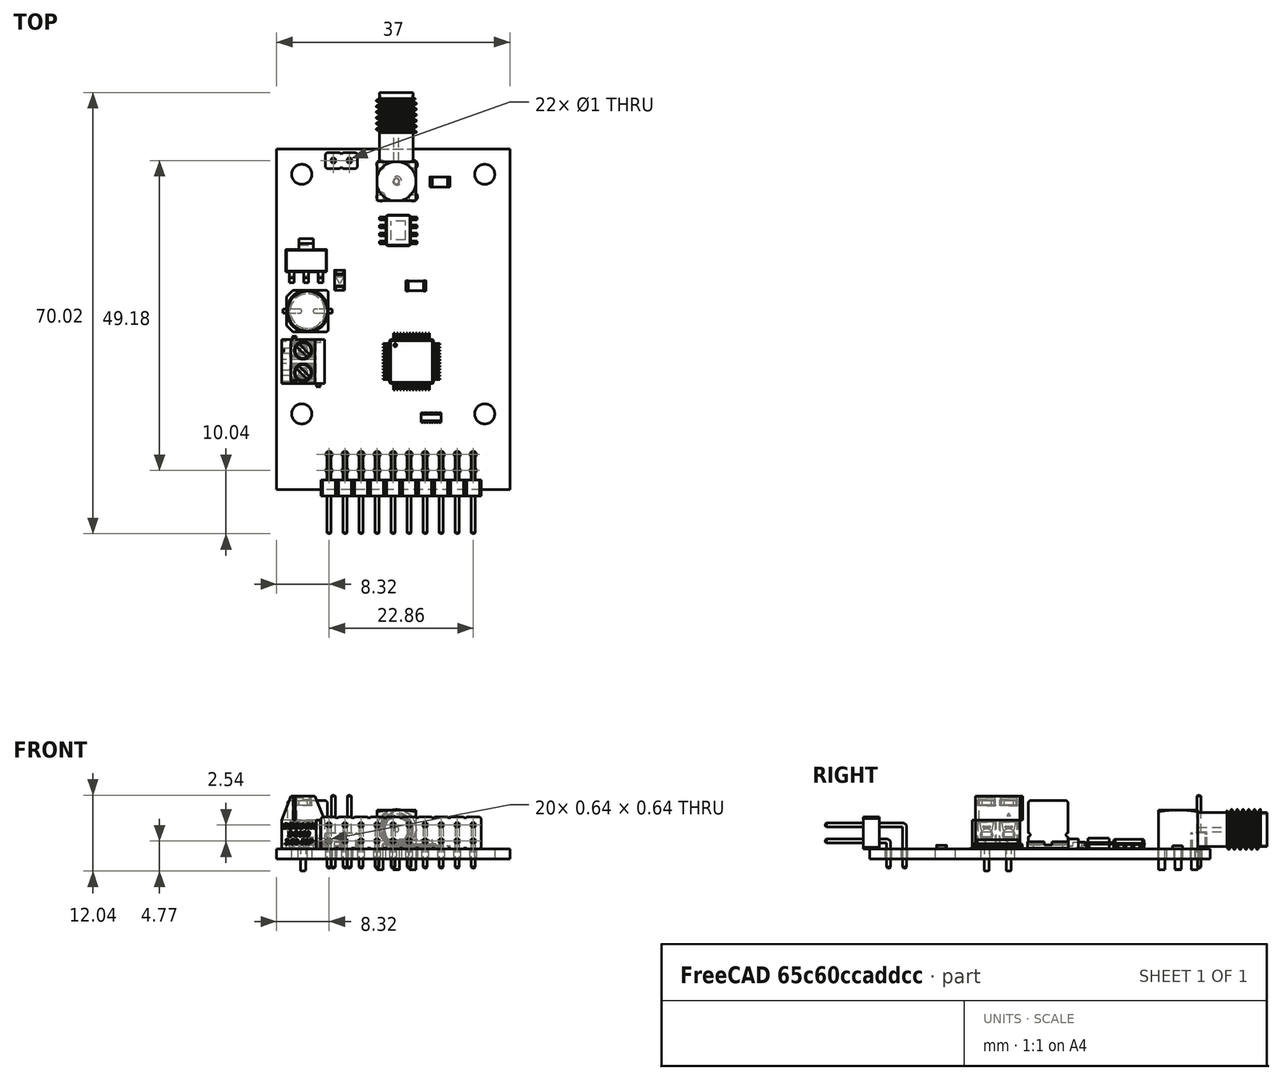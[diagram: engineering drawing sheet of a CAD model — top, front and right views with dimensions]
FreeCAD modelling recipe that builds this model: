
FCSTD DOCUMENT  (FreeCAD 1.0R39109 (Git))
Label: ADC
License: All rights reserved
LicenseURL: https://en.wikipedia.org/wiki/All_rights_reserved
objects: App::Link×34, Part::Feature×13, App::Part×4, PartDesign::CoordinateSystem×1, Sketcher::SketchObject×1
note: 16 computed .brp shape members not serialized (recipe doc carries the construction recipe); baked Part::Feature solids carry a one-line shape summary decoded from their .brp

FEATURE [PartDesign::CoordinateSystem] Local_CS_3770
  AttacherType = Attacher::AttachEngine3D
  MapMode = 2
FEATURE [Part::Feature] Pcb_3770
  Placement = pos=(-93.74,138.54,0) rot=(0,0,1;0rad)
  shape: bbox 37 x 54 x 1.6 mm, 39 faces (baked)
FEATURE [Sketcher::SketchObject] PCB_Sketch_3770
  ArcFitTolerance = 1e-06
  FullyConstrained = false
  MakeInternals = false
  sketch-geometry (4):
    g0: LineSegment StartX=-31.24 StartY=51.04 StartZ=0 EndX=5.76 EndY=51.04 EndZ=0
    g1: LineSegment StartX=5.76 StartY=51.04 StartZ=0 EndX=5.76 EndY=-2.96 EndZ=0
    g2: LineSegment StartX=5.76 StartY=-2.96 StartZ=0 EndX=-31.24 EndY=-2.96 EndZ=0
    g3: LineSegment StartX=-31.24 StartY=-2.96 StartZ=0 EndX=-31.24 EndY=51.04 EndZ=0
  constraints (4):
    c: Coincident(g2,g3)
    c: Coincident(g0,g3)
    c: Coincident(g1,g2)
    c: Coincident(g0,g1)
FEATURE [App::Part] Board_Geoms_3770
  Group = -> [Pcb_3770,PCB_Sketch_3770]
  Origin = -> Origin
FEATURE [Part::Feature] Shape  label="REF_R_1206_3216Metric_301ddd0c36ed"
  Placement = pos=(-5.34,45.84,0) rot=(0,0,1;0rad)
  shape: bbox 3.2 x 1.6 x 0.55 mm, 26 faces (baked)
FEATURE [App::Link] REF_R_1206_3216Metric_301ddd0c36ed_ln_  label="REF_REF_R_1206_3216Metric_70df84f1ae34"
  LinkPlacement = pos=(-22.84,41.94,0) rot=(0,0,1;1.5708rad)
  LinkedObject = -> Shape
  Placement = pos=(-22.84,41.94,0) rot=(0,0,1;1.5708rad)
FEATURE [App::Link] REF_R_1206_3216Metric_301ddd0c36ed_ln_001  label="REF_REF_R_1206_3216Metric_a6f854153131"
  LinkPlacement = pos=(1.16,14.24,0) rot=(0,0,1;0rad)
  LinkedObject = -> Shape
  Placement = pos=(1.16,14.24,0) rot=(0,0,1;0rad)
FEATURE [Part::Feature] Shape001  label="REF_C_1206_3216Metric_e221a3b84079"
  Placement = pos=(-9.14,29.34,0) rot=(0,0,1;0rad)
  shape: bbox 3.2 x 1.6 x 1.6 mm, 28 faces (baked)
FEATURE [App::Link] REF_R_1206_3216Metric_301ddd0c36ed_ln_002  label="REF_REF_R_1206_3216Metric_a0f92e46f677"
  LinkPlacement = pos=(-10.64,32.94,0) rot=(0,0,1;1.5708rad)
  LinkedObject = -> Shape
  Placement = pos=(-10.64,32.94,0) rot=(0,0,1;1.5708rad)
FEATURE [Part::Feature] Shape002  label="REF_CP_Elec_63x77_d1b758cef271"
  Placement = pos=(-26.34,25.34,0) rot=(0,0,1;0rad)
  shape: bbox 8.606 x 8.603 x 7.7 mm, 41 faces (baked)
FEATURE [App::Link] REF_R_1206_3216Metric_301ddd0c36ed_ln_003  label="REF_REF_R_1206_3216Metric_1b9d2568f397"
  LinkPlacement = pos=(-20.24,41.94,0) rot=(0,0,1;1.5708rad)
  LinkedObject = -> Shape
  Placement = pos=(-20.24,41.94,0) rot=(0,0,1;1.5708rad)
FEATURE [Part::Feature] Shape003  label="REF_SOIC-8-1EP_3.9x4.9mm_P1.27mm_EP2.29x3mm_4b1fed1f54c1"
  Placement = pos=(-11.94,38.14,0) rot=(0,0,1;3.14159rad)
  shape: bbox 6 x 4.9 x 1.55 mm, 152 faces (baked)
FEATURE [App::Link] REF_C_1206_3216Metric_e221a3b84079_ln_  label="REF_REF_C_1206_3216Metric_3e90dc9b15e9"
  LinkPlacement = pos=(-1.24,27.14,0) rot=(0,0,1;0rad)
  LinkedObject = -> Shape001
  Placement = pos=(-1.24,27.14,0) rot=(0,0,1;0rad)
FEATURE [App::Link] REF_C_1206_3216Metric_e221a3b84079_ln_001  label="REF_REF_C_1206_3216Metric_f21636db2d26"
  LinkPlacement = pos=(-7.14,24.54,0) rot=(0,0,1;0rad)
  LinkedObject = -> Shape001
  Placement = pos=(-7.14,24.54,0) rot=(0,0,1;0rad)
FEATURE [App::Link] REF_C_1206_3216Metric_e221a3b84079_ln_002  label="REF_REF_C_1206_3216Metric_18777c7b1951"
  LinkPlacement = pos=(-10.74,25.34,0) rot=(0,0,1;1.5708rad)
  LinkedObject = -> Shape001
  Placement = pos=(-10.74,25.34,0) rot=(0,0,1;1.5708rad)
FEATURE [App::Link] REF_R_1206_3216Metric_301ddd0c36ed_ln_004  label="REF_REF_R_1206_3216Metric_5a7a546a1d58"
  LinkPlacement = pos=(0.96,22.24,0) rot=(0,0,1;0rad)
  LinkedObject = -> Shape
  Placement = pos=(0.96,22.24,0) rot=(0,0,1;0rad)
FEATURE [App::Link] REF_R_1206_3216Metric_301ddd0c36ed_ln_005  label="REF_REF_R_1206_3216Metric_6cf90c486473"
  LinkPlacement = pos=(-18.04,8.54,0) rot=(0,0,1;1.5708rad)
  LinkedObject = -> Shape
  Placement = pos=(-18.04,8.54,0) rot=(0,0,1;1.5708rad)
FEATURE [Part::Feature] Shape004  label="REF_LED_1206_3216Metric_2fccf6a8874c"
  Placement = pos=(-21.24,30.24,0) rot=(0,0,1;1.5708rad)
  shape: bbox 1.6 x 3.2 x 1.1 mm, 50 faces (baked)
FEATURE [Part::Feature] Shape005  label="REF_PinHeader_1x02_P254mm_Vertical_da5b8ef0d3b1"
  Placement = pos=(-22.24,49.24,0) rot=(0,0,1;1.5708rad)
  shape: bbox 5.08 x 2.54 x 11.54 mm, 52 faces (baked)
FEATURE [App::Link] REF_C_1206_3216Metric_e221a3b84079_ln_003  label="REF_REF_C_1206_3216Metric_64c44e93813f"
  LinkPlacement = pos=(-16.44,19.84,0) rot=(0,0,1;1.5708rad)
  LinkedObject = -> Shape001
  Placement = pos=(-16.44,19.84,0) rot=(0,0,1;1.5708rad)
FEATURE [App::Link] REF_R_1206_3216Metric_301ddd0c36ed_ln_006  label="REF_REF_R_1206_3216Metric_3b6dfaf97a83"
  LinkPlacement = pos=(-5.34,48.74,0) rot=(0,0,1;0rad)
  LinkedObject = -> Shape
  Placement = pos=(-5.34,48.74,0) rot=(0,0,1;0rad)
FEATURE [App::Link] REF_R_1206_3216Metric_301ddd0c36ed_ln_007  label="REF_REF_R_1206_3216Metric_8c0fe4bfaf64"
  LinkPlacement = pos=(0.96,19.44,0) rot=(0,0,1;0rad)
  LinkedObject = -> Shape
  Placement = pos=(0.96,19.44,0) rot=(0,0,1;0rad)
FEATURE [App::Link] REF_C_1206_3216Metric_e221a3b84079_ln_004  label="REF_REF_C_1206_3216Metric_99c8eecee891"
  LinkPlacement = pos=(-13.14,25.34,0) rot=(0,0,1;1.5708rad)
  LinkedObject = -> Shape001
  Placement = pos=(-13.14,25.34,0) rot=(0,0,1;1.5708rad)
FEATURE [App::Link] REF_R_1206_3216Metric_301ddd0c36ed_ln_008  label="REF_REF_R_1206_3216Metric_75b0c98a4610"
  LinkPlacement = pos=(-6.34,35.04,0) rot=(0,0,1;1.5708rad)
  LinkedObject = -> Shape
  Placement = pos=(-6.34,35.04,0) rot=(0,0,1;1.5708rad)
FEATURE [App::Link] REF_C_1206_3216Metric_e221a3b84079_ln_005  label="REF_REF_C_1206_3216Metric_2542e80cc9ef"
  LinkPlacement = pos=(-4.74,29.34,0) rot=(0,0,1;0rad)
  LinkedObject = -> Shape001
  Placement = pos=(-4.74,29.34,0) rot=(0,0,1;0rad)
FEATURE [App::Link] REF_R_1206_3216Metric_301ddd0c36ed_ln_009  label="REF_REF_R_1206_3216Metric_7b8190f97f6e"
  LinkPlacement = pos=(-6.44,39.74,0) rot=(0,0,1;1.5708rad)
  LinkedObject = -> Shape
  Placement = pos=(-6.44,39.74,0) rot=(0,0,1;1.5708rad)
FEATURE [Part::Feature] Shape006  label="REF_R_Array_Concave_4x0603_6ebfddd59be7"
  Placement = pos=(-6.74,8.44,0) rot=(0,0,1;1.5708rad)
  shape: bbox 3.2 x 1.6 x 0.6 mm, 140 faces (baked)
FEATURE [App::Link] REF_C_1206_3216Metric_e221a3b84079_ln_006  label="REF_REF_C_1206_3216Metric_ddc78717e179"
  LinkPlacement = pos=(-2.54,20.84,0) rot=(0,0,1;1.5708rad)
  LinkedObject = -> Shape001
  Placement = pos=(-2.54,20.84,0) rot=(0,0,1;1.5708rad)
FEATURE [App::Link] REF_C_1206_3216Metric_e221a3b84079_ln_007  label="REF_REF_C_1206_3216Metric_0f9f458e9312"
  LinkPlacement = pos=(-26.64,39.44,0) rot=(0,0,1;0rad)
  LinkedObject = -> Shape001
  Placement = pos=(-26.64,39.44,0) rot=(0,0,1;0rad)
FEATURE [App::Link] REF_R_1206_3216Metric_301ddd0c36ed_ln_010  label="REF_REF_R_1206_3216Metric_e40d589cdbd9"
  LinkPlacement = pos=(1.06,17.04,0) rot=(0,0,1;0rad)
  LinkedObject = -> Shape
  Placement = pos=(1.06,17.04,0) rot=(0,0,1;0rad)
FEATURE [App::Link] REF_R_Array_Concave_4x0603_6ebfddd59be7_ln_  label="REF_REF_R_Array_Concave_4x0603_c1e9b6bea166"
  LinkPlacement = pos=(-10.74,8.44,0) rot=(0,0,1;1.5708rad)
  LinkedObject = -> Shape006
  Placement = pos=(-10.74,8.44,0) rot=(0,0,1;1.5708rad)
FEATURE [App::Link] REF_C_1206_3216Metric_e221a3b84079_ln_008  label="REF_REF_C_1206_3216Metric_0664d0335a5c"
  LinkPlacement = pos=(-2.54,15.14,0) rot=(0,0,1;1.5708rad)
  LinkedObject = -> Shape001
  Placement = pos=(-2.54,15.14,0) rot=(0,0,1;1.5708rad)
FEATURE [App::Link] REF_R_1206_3216Metric_301ddd0c36ed_ln_011  label="REF_REF_R_1206_3216Metric_d8d0c14688f2"
  LinkPlacement = pos=(-17.54,34.94,0) rot=(0,0,1;1.5708rad)
  LinkedObject = -> Shape
  Placement = pos=(-17.54,34.94,0) rot=(0,0,1;1.5708rad)
FEATURE [App::Link] REF_R_1206_3216Metric_301ddd0c36ed_ln_012  label="REF_REF_R_1206_3216Metric_336c34d7c97d"
  LinkPlacement = pos=(-3.84,8.34,0) rot=(0,0,1;1.5708rad)
  LinkedObject = -> Shape
  Placement = pos=(-3.84,8.34,0) rot=(0,0,1;1.5708rad)
FEATURE [Part::Feature] Shape007  label="REF_DG350-3.96-02P-12-00AH_5fb89e4e64b6"
  Placement = pos=(-23.64,20.84,0) rot=(0.57735,-0.57735,-0.57735;2.0944rad)
  shape: bbox 6.8 x 8 x 11.9 mm, 434 faces (baked)
FEATURE [App::Link] REF_C_1206_3216Metric_e221a3b84079_ln_009  label="REF_REF_C_1206_3216Metric_c52bb9b8716f"
  LinkPlacement = pos=(-3.64,39.84,0) rot=(0,0,1;1.5708rad)
  LinkedObject = -> Shape001
  Placement = pos=(-3.64,39.84,0) rot=(0,0,1;1.5708rad)
FEATURE [App::Link] REF_R_1206_3216Metric_301ddd0c36ed_ln_013  label="REF_REF_R_1206_3216Metric_975d7f625023"
  LinkPlacement = pos=(-17.14,25.54,0) rot=(0,0,1;1.5708rad)
  LinkedObject = -> Shape
  Placement = pos=(-17.14,25.54,0) rot=(0,0,1;1.5708rad)
FEATURE [App::Link] REF_C_1206_3216Metric_e221a3b84079_ln_010  label="REF_REF_C_1206_3216Metric_4ccb42aa522b"
  LinkPlacement = pos=(-7.14,26.84,0) rot=(0,0,1;0rad)
  LinkedObject = -> Shape001
  Placement = pos=(-7.14,26.84,0) rot=(0,0,1;0rad)
FEATURE [Part::Feature] Shape008  label="REF_SOT_223_e5314abddc11"
  Placement = pos=(-26.54,33.34,0) rot=(0,0,1;1.5708rad)
  shape: bbox 6.5 x 7 x 1.7 mm, 78 faces (baked)
FEATURE [Part::Feature] Shape009  label="REF_HJ-Tech-HJ-SMA175_5e94955ffa82"
  Placement = pos=(-9.14,49.04,0) rot=(0,0.707107,0.707107;3.14159rad)
  shape: bbox 8.673 x 18.44 x 9.575 mm, 56 faces (baked)
FEATURE [App::Link] REF_R_1206_3216Metric_301ddd0c36ed_ln_014  label="REF_REF_R_1206_3216Metric_01a2f680d26f"
  LinkPlacement = pos=(-21.44,34.74,0) rot=(0,0,1;1.5708rad)
  LinkedObject = -> Shape
  Placement = pos=(-21.44,34.74,0) rot=(0,0,1;1.5708rad)
FEATURE [Part::Feature] Shape010  label="REF_PinHeader_2x10_P254mm_Horizontal_88ad88291e13"
  Placement = pos=(-0.06,2.6,0) rot=(0,0,-1;1.5708rad)
  shape: bbox 25.4 x 12.9 x 8.08 mm, 484 faces (baked)
FEATURE [Part::Feature] Shape011  label="REF_LQFP_48_7x7mm_P05mm_d06fefb0920b"
  Placement = pos=(-9.84,17.34,0) rot=(0,0,1;0rad)
  shape: bbox 9 x 9 x 1.5 mm, 764 faces (baked)
FEATURE [App::Link] REF_R_1206_3216Metric_301ddd0c36ed_ln_015  label="REF_REF_R_1206_3216Metric_06fab732c749"
  LinkPlacement = pos=(-17.44,39.54,0) rot=(0,0,1;1.5708rad)
  LinkedObject = -> Shape
  Placement = pos=(-17.44,39.54,0) rot=(0,0,1;1.5708rad)
FEATURE [App::Link] REF_R_1206_3216Metric_301ddd0c36ed_ln_016  label="REF_REF_R_1206_3216Metric_0ba6753cf2ae"
  LinkPlacement = pos=(-5.44,43.24,0) rot=(0,0,1;0rad)
  LinkedObject = -> Shape
  Placement = pos=(-5.44,43.24,0) rot=(0,0,1;0rad)
FEATURE [App::Link] REF_R_1206_3216Metric_301ddd0c36ed_ln_017  label="REF_REF_R_1206_3216Metric_f8758bee8265"
  LinkPlacement = pos=(-13.04,32.94,0) rot=(0,0,1;1.5708rad)
  LinkedObject = -> Shape
  Placement = pos=(-13.04,32.94,0) rot=(0,0,1;1.5708rad)
FEATURE [App::Link] REF_R_Array_Concave_4x0603_6ebfddd59be7_ln_001  label="REF_REF_R_Array_Concave_4x0603_4768bc114470"
  LinkPlacement = pos=(-14.74,8.44,0) rot=(0,0,1;1.5708rad)
  LinkedObject = -> Shape006
  Placement = pos=(-14.74,8.44,0) rot=(0,0,1;1.5708rad)
FEATURE [App::Link] REF_C_1206_3216Metric_e221a3b84079_ln_011  label="REF_REF_C_1206_3216Metric_aac49cf074a5"
  LinkPlacement = pos=(-1.14,24.64,0) rot=(0,0,1;0rad)
  LinkedObject = -> Shape001
  Placement = pos=(-1.14,24.64,0) rot=(0,0,1;0rad)
FEATURE [App::Link] REF_C_1206_3216Metric_e221a3b84079_ln_012  label="REF_REF_C_1206_3216Metric_d76365948289"
  LinkPlacement = pos=(-3.74,35.04,0) rot=(0,0,1;1.5708rad)
  LinkedObject = -> Shape001
  Placement = pos=(-3.74,35.04,0) rot=(0,0,1;1.5708rad)
FEATURE [App::Link] REF_R_1206_3216Metric_301ddd0c36ed_ln_018  label="REF_REF_R_1206_3216Metric_e63bd7cbb3e0"
  LinkPlacement = pos=(-17.34,44.44,0) rot=(0,0,1;1.5708rad)
  LinkedObject = -> Shape
  Placement = pos=(-17.34,44.44,0) rot=(0,0,1;1.5708rad)
FEATURE [App::Part] Top_3770
  Group = -> [Shape,REF_R_1206_3216Metric_301ddd0c36ed_ln_,REF_R_1206_3216Metric_301ddd0c36ed_ln_001,Shape001,REF_R_1206_3216Metric_301ddd0c36ed_ln_002,Shape002,REF_R_1206_3216Metric_301ddd0c36ed_ln_003,Shape003,REF_C_1206_3216Metric_e221a3b84079_ln_,REF_C_1206_3216Metric_e221a3b84079_ln_001,REF_C_1206_3216Metric_e221a3b84079_ln_002,REF_R_1206_3216Metric_301ddd0c36ed_ln_004,+34 more]
  Origin = -> Origin003
FEATURE [App::Part] Step_Models_3770
  Group = -> [Top_3770]
  Origin = -> Origin002
FEATURE [App::Part] Board_3770  label="adc"
  Group = -> [Local_CS_3770,Board_Geoms_3770,Step_Models_3770]
  Origin = -> Origin001
